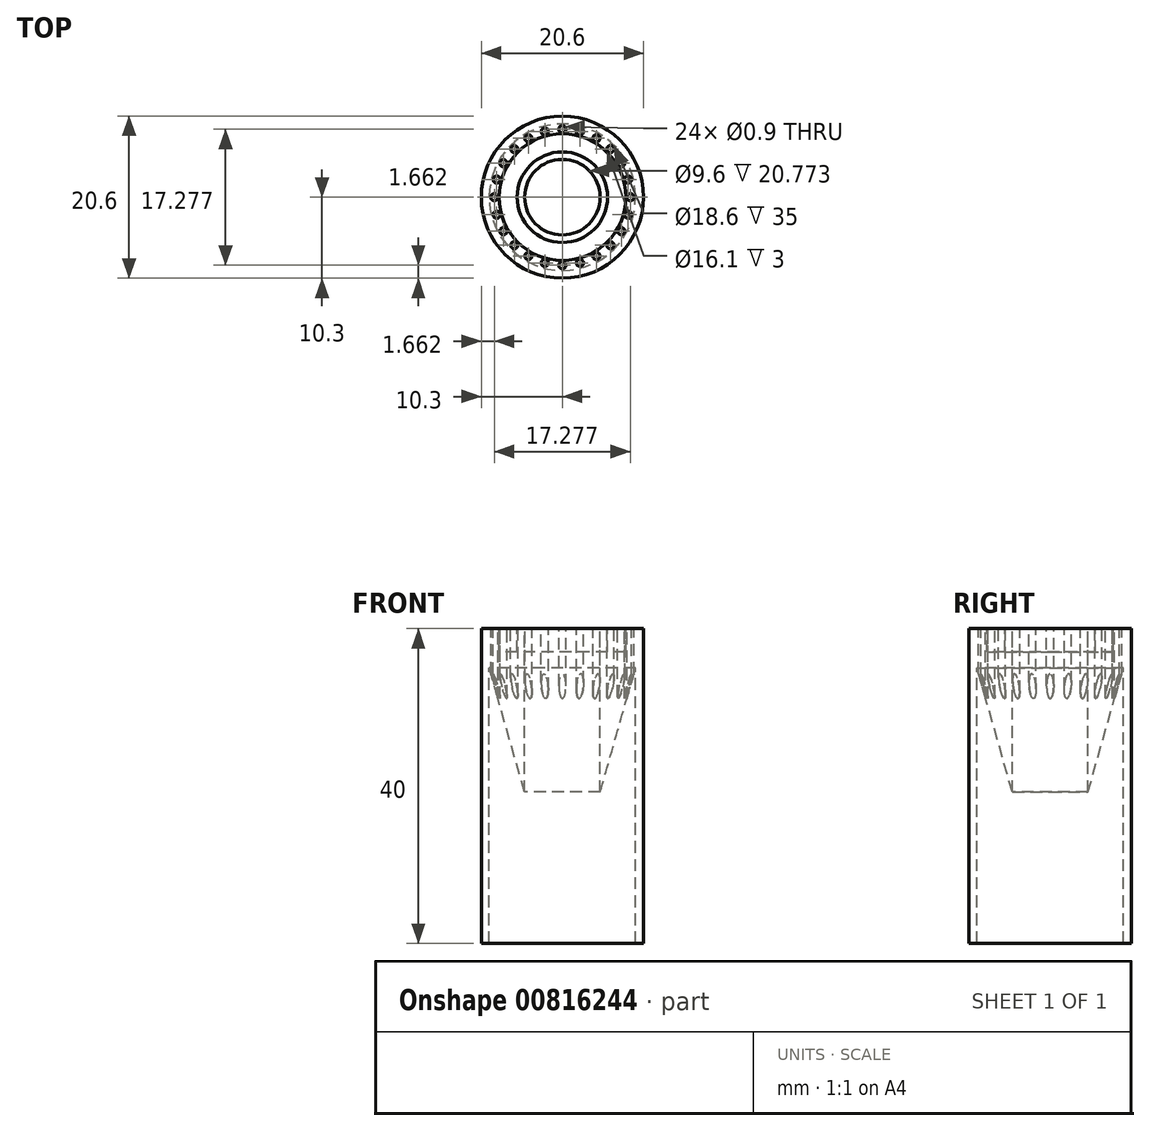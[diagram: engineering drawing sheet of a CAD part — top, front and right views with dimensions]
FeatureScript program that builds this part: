
annotation { "Feature Type Name" : "Feature", "Feature Type Description" : "" }
export const myFeature = defineFeature(function(context is Context, id is Id, definition is map)
    precondition{}
    {
        {
            var Q0;
            Q0=qCreatedBy(makeId("Front.planeOp"),FACE);
            var sketch = newSketch(context, id + "F0", { "sketchPlane" : qUnion([Q0])});
            skLineSegment(sketch, "E0", {"start": v(0, 40) * mm, "end": v(0, 0) * mm, "construction": true});
            skLineSegment(sketch, "E1", {"start": v(0, 0) * mm, "end": v(10.5, 0) * mm, "construction": true});
            skLineSegment(sketch, "E2", {"start": v(10.3, 0) * mm, "end": v(10.3, 40) * mm});
            skLineSegment(sketch, "E3", {"start": v(9.3, 0) * mm, "end": v(9.3, 35) * mm});
            skLineSegment(sketch, "E4", {"start": v(9.3, 35) * mm, "end": v(4.8, 19.23) * mm});
            skLineSegment(sketch, "E5", {"start": v(4.8, 19.23) * mm, "end": v(4.8, 40) * mm});
            skLineSegment(sketch, "E6", {"start": v(10.3, 40) * mm, "end": v(4.8, 40) * mm});
            skLineSegment(sketch, "E7", {"start": v(10.5, 0) * mm, "end": v(9.3, 0) * mm});
            skSolve(sketch);
        }
        {
            var Q0;
            Q0 = qSketchRegion(id + "F0", true);
            var Q1;
            Q1=sQuery(id+"F0.wireOp",EDGE,"E0");
            revolve(context, id + "F1", {"surfaceOperationType" : NewSurfaceOperationType.NEW, "entities" : qUnion([Q0]), "axis" : qUnion([Q1]), "revolveType" : RevolveType.FULL});
        }
        {
            var Q0;
            Q0=makeQuery(id+"F1.opRevolve","SWEPT_FACE",FACE,{"disambiguationData":[OSD([sQuery(id+"F0.wireOp",EDGE,"E6")])]});
            var sketch = newSketch(context, id + "F2", { "sketchPlane" : qUnion([Q0])});
            skCircle(sketch, "E8", {"center": v(0, 0) * mm, "radius": 8.05 * mm});
            skCircle(sketch, "E9", {"center": v(0, 0) * mm, "radius": 5.75 * mm});
            skSolve(sketch);
        }
        {
            var Q0;
            Q0 = qSketchRegion(id + "F2", true);
            extrude(context, id + "F3", {"entities" : qUnion([Q0]), "operationType" : NewBodyOperationType.REMOVE, "oppositeDirection" : true, "depth" : 3 * mm, "offsetDistance" : 25 * mm});
        }
        {
            var Q0;
            Q0=makeQuery(id+"F3.boolean.opBoolean","SPLIT",FACE,{"disambiguationData":[TD([makeQuery(id+"F1.opRevolve","SWEPT_FACE",FACE,{"disambiguationData":[OSD([sQuery(id+"F0.wireOp",EDGE,"E2")])]})])],"derivedFrom":makeQuery(id+"F1.opRevolve","SWEPT_FACE",FACE,{"disambiguationData":[OSD([sQuery(id+"F0.wireOp",EDGE,"E6")])]})});
            var sketch = newSketch(context, id + "F4", { "sketchPlane" : qUnion([Q0])});
            skCircle(sketch, "E10", {"center": v(0, 8.64) * mm, "radius": 0.45 * mm});
            skCircle(sketch, "E11.1.0", {"center": v(-2.24, 8.34) * mm, "radius": 0.45 * mm});
            skCircle(sketch, "E11.2.0", {"center": v(-4.32, 7.48) * mm, "radius": 0.45 * mm});
            skCircle(sketch, "E11.3.0", {"center": v(-6.1, 6.1) * mm, "radius": 0.45 * mm});
            skCircle(sketch, "E11.4.0", {"center": v(-7.48, 4.32) * mm, "radius": 0.45 * mm});
            skCircle(sketch, "E11.5.0", {"center": v(-8.34, 2.24) * mm, "radius": 0.45 * mm});
            skCircle(sketch, "E11.6.0", {"center": v(-8.64, 0) * mm, "radius": 0.45 * mm});
            skCircle(sketch, "E11.7.0", {"center": v(-8.34, -2.24) * mm, "radius": 0.45 * mm});
            skCircle(sketch, "E11.8.0", {"center": v(-7.48, -4.32) * mm, "radius": 0.45 * mm});
            skCircle(sketch, "E11.9.0", {"center": v(-6.1, -6.1) * mm, "radius": 0.45 * mm});
            skCircle(sketch, "E11.10.0", {"center": v(-4.32, -7.48) * mm, "radius": 0.45 * mm});
            skCircle(sketch, "E11.11.0", {"center": v(-2.24, -8.34) * mm, "radius": 0.45 * mm});
            skCircle(sketch, "E11.12.0", {"center": v(0, -8.64) * mm, "radius": 0.45 * mm});
            skCircle(sketch, "E11.13.0", {"center": v(2.24, -8.34) * mm, "radius": 0.45 * mm});
            skCircle(sketch, "E11.14.0", {"center": v(4.32, -7.48) * mm, "radius": 0.45 * mm});
            skCircle(sketch, "E11.15.0", {"center": v(6.1, -6.1) * mm, "radius": 0.45 * mm});
            skCircle(sketch, "E11.16.0", {"center": v(7.48, -4.32) * mm, "radius": 0.45 * mm});
            skCircle(sketch, "E11.17.0", {"center": v(8.34, -2.24) * mm, "radius": 0.45 * mm});
            skCircle(sketch, "E11.18.0", {"center": v(8.64, 0) * mm, "radius": 0.45 * mm});
            skCircle(sketch, "E11.19.0", {"center": v(8.34, 2.24) * mm, "radius": 0.45 * mm});
            skCircle(sketch, "E11.20.0", {"center": v(7.48, 4.32) * mm, "radius": 0.45 * mm});
            skCircle(sketch, "E11.21.0", {"center": v(6.1, 6.1) * mm, "radius": 0.45 * mm});
            skCircle(sketch, "E11.22.0", {"center": v(4.32, 7.48) * mm, "radius": 0.45 * mm});
            skCircle(sketch, "E11.23.0", {"center": v(2.24, 8.34) * mm, "radius": 0.45 * mm});
            skPoint(sketch, "E11.center", {"position": v(0, 0) * mm});
            skSolve(sketch);
        }
        {
            var Q0;
            Q0 = qSketchRegion(id + "F4", true);
            extrude(context, id + "F5", {"entities" : qUnion([Q0]), "operationType" : NewBodyOperationType.REMOVE, "oppositeDirection" : true, "depth" : 25 * mm, "offsetDistance" : 25 * mm});
        }
    });
